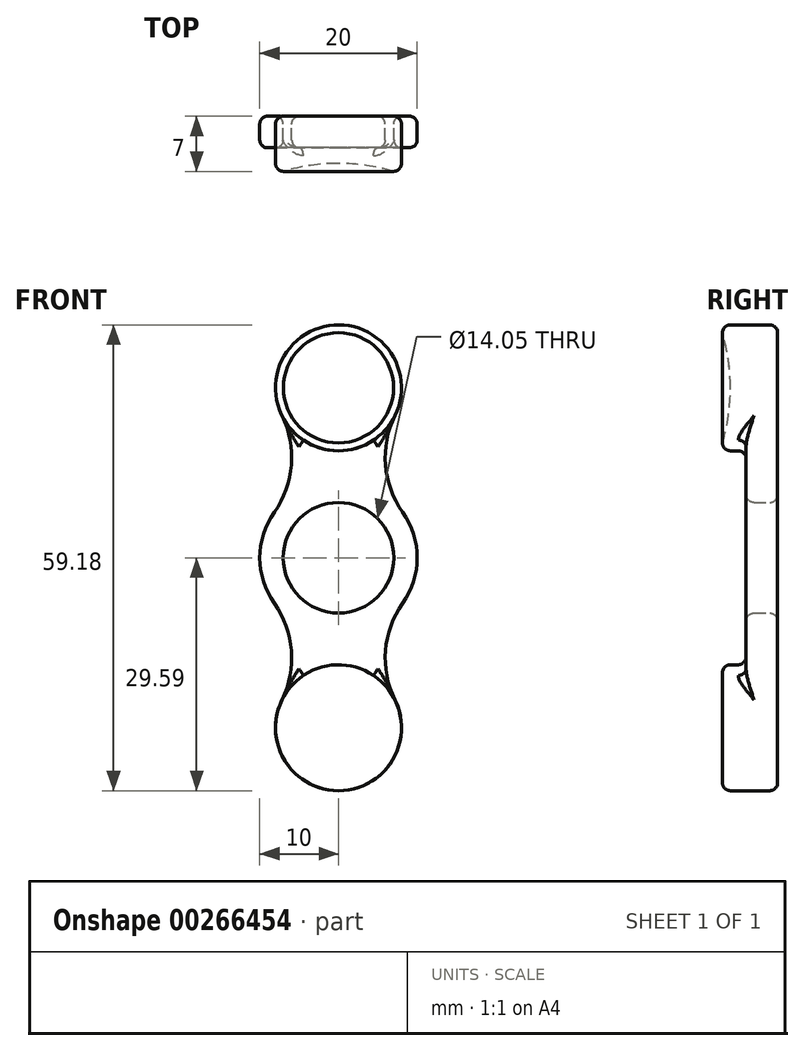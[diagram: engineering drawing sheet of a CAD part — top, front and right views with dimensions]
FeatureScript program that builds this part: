
annotation { "Feature Type Name" : "Feature", "Feature Type Description" : "" }
export const myFeature = defineFeature(function(context is Context, id is Id, definition is map)
    precondition{}
    {
        {
            var Q0;
            Q0=qCreatedBy(makeId("Front.planeOp"),FACE);
            var sketch = newSketch(context, id + "F7", { "sketchPlane" : qUnion([Q0])});
            skCircle(sketch, "E0", {"center": v(0, 0) * mm, "radius": 7.03 * mm});
            skArc(sketch, "E1", {"start": v(8.15, 5.8) * mm, "mid": v(10, 0) * mm, "end": v(8.15, -5.8) * mm});
            skLineSegment(sketch, "E2", {"start": v(0, 0) * mm, "end": v(0, 21.59) * mm, "construction": true});
            skArc(sketch, "E3", {"start": v(7.17, 18.05) * mm, "mid": v(0, 29.59) * mm, "end": v(-7.17, 18.05) * mm});
            skArc(sketch, "E4", {"start": v(-8.15, 5.8) * mm, "mid": v(-5.97, 11.79) * mm, "end": v(-7.17, 18.05) * mm});
            skArc(sketch, "E5.MirrorCS", {"start": v(8.15, 5.8) * mm, "mid": v(5.97, 11.79) * mm, "end": v(7.17, 18.05) * mm});
            skLineSegment(sketch, "E6", {"start": v(10, 0) * mm, "end": v(-10, 0) * mm, "construction": true});
            skArc(sketch, "E7.MirrorCS", {"start": v(7.17, -18.05) * mm, "mid": v(0, -29.59) * mm, "end": v(-7.17, -18.05) * mm});
            skArc(sketch, "E8.MirrorCS", {"start": v(-8.15, -5.8) * mm, "mid": v(-5.97, -11.79) * mm, "end": v(-7.17, -18.05) * mm});
            skArc(sketch, "E9.MirrorCS", {"start": v(8.15, -5.8) * mm, "mid": v(5.97, -11.79) * mm, "end": v(7.17, -18.05) * mm});
            skArc(sketch, "E10.trimOffspring", {"start": v(-8.15, -5.8) * mm, "mid": v(-10, 0) * mm, "end": v(-8.15, 5.8) * mm});
            skSolve(sketch);
        }
        {
            var Q0;
            Q0=makeQuery(id+"F7.imprint","IMPRINT",FACE,{"disambiguationData":[TD([[makeQuery(id+"F7.imprint","IMPRINT",EDGE,{"derivedFrom":sQuery(id+"F7.wireOp",EDGE,"E0")}),-1.0]])]});
            extrude(context, id + "F0", {"entities" : qUnion([Q0]), "depth" : 4 * mm});
        }
        {
            var Q0;
            Q0=makeQuery(id+"F0.opExtrude","CAP_FACE",FACE,{"disambiguationData":[OSD([sQuery(id+"F7.wireOp",EDGE,"E0"),sQuery(id+"F7.wireOp",EDGE,"E1"),sQuery(id+"F7.wireOp",EDGE,"E3"),sQuery(id+"F7.wireOp",EDGE,"E4"),sQuery(id+"F7.wireOp",EDGE,"E5.MirrorCS"),sQuery(id+"F7.wireOp",EDGE,"E7.MirrorCS"),sQuery(id+"F7.wireOp",EDGE,"E8.MirrorCS"),sQuery(id+"F7.wireOp",EDGE,"E9.MirrorCS"),sQuery(id+"F7.wireOp",EDGE,"E10.trimOffspring")])],"isStart":false});
            var sketch = newSketch(context, id + "F1", { "sketchPlane" : qUnion([Q0])});
            skCircle(sketch, "E11", {"center": v(0, -21.59) * mm, "radius": 8 * mm});
            skCircle(sketch, "E12", {"center": v(0, 21.59) * mm, "radius": 8 * mm});
            skSolve(sketch);
        }
        {
            var Q0;
            Q0 = qSketchRegion(id + "F1", true);
            extrude(context, id + "F2", {"entities" : qUnion([Q0]), "operationType" : NewBodyOperationType.ADD, "depth" : 3 * mm});
        }
        {
            var Q0;
            Q0=makeQuery(id+"F2.opExtrude","CAP_EDGE",EDGE,{"disambiguationData":[OSD([sQuery(id+"F1.wireOp",EDGE,"E12")])],"isStart":false});
            var Q1;
            Q1=makeQuery(id+"F2.opExtrude","CAP_EDGE",EDGE,{"disambiguationData":[OSD([sQuery(id+"F1.wireOp",EDGE,"E11")])],"isStart":false});
            fillet(context, id + "F3", {"entities" : qUnion([Q0, Q1]), "radius" : 1 * mm, "tangentPropagation" : true, "allowEdgeOverflow" : false});
        }
        {
            var Q0;
            Q0=makeQuery(id+"F0.opExtrude","CAP_FACE",FACE,{"disambiguationData":[OSD([sQuery(id+"F7.wireOp",EDGE,"E0"),sQuery(id+"F7.wireOp",EDGE,"E1"),sQuery(id+"F7.wireOp",EDGE,"E3"),sQuery(id+"F7.wireOp",EDGE,"E4"),sQuery(id+"F7.wireOp",EDGE,"E5.MirrorCS"),sQuery(id+"F7.wireOp",EDGE,"E7.MirrorCS"),sQuery(id+"F7.wireOp",EDGE,"E8.MirrorCS"),sQuery(id+"F7.wireOp",EDGE,"E9.MirrorCS"),sQuery(id+"F7.wireOp",EDGE,"E10.trimOffspring")])],"isStart":true});
            var Q1;
            Q1=makeQuery(id+"F0.opExtrude","CAP_FACE",FACE,{"disambiguationData":[OSD([sQuery(id+"F7.wireOp",EDGE,"E0"),sQuery(id+"F7.wireOp",EDGE,"E1"),sQuery(id+"F7.wireOp",EDGE,"E3"),sQuery(id+"F7.wireOp",EDGE,"E4"),sQuery(id+"F7.wireOp",EDGE,"E5.MirrorCS"),sQuery(id+"F7.wireOp",EDGE,"E7.MirrorCS"),sQuery(id+"F7.wireOp",EDGE,"E8.MirrorCS"),sQuery(id+"F7.wireOp",EDGE,"E9.MirrorCS"),sQuery(id+"F7.wireOp",EDGE,"E10.trimOffspring")])],"isStart":false});
            var Q2;
            Q2=makeQuery(id+"F0.opExtrude","CAP_EDGE",EDGE,{"disambiguationData":[OSD([sQuery(id+"F7.wireOp",EDGE,"E0")])],"isStart":false});
            var Q3;
            Q3=makeQuery(id+"F0.opExtrude","CAP_EDGE",EDGE,{"disambiguationData":[OSD([sQuery(id+"F7.wireOp",EDGE,"E0")])],"isStart":true});
            fillet(context, id + "F4", {"entities" : qUnion([Q0, Q1, Q2, Q3]), "radius" : 1 * mm, "tangentPropagation" : true, "allowEdgeOverflow" : false});
        }
        {
            var Q0;
            Q0=qCreatedBy(makeId("Right.planeOp"),FACE);
            var sketch = newSketch(context, id + "F5", { "sketchPlane" : qUnion([Q0])});
            skLineSegment(sketch, "E13.0", {"start": v(-7, 14.6) * mm, "end": v(-7, 28.59) * mm});
            skLineSegment(sketch, "E14", {"start": v(0, 0) * mm, "end": v(-21.03, 0) * mm, "construction": true});
            skLineSegment(sketch, "E15", {"start": v(-7, 21.59) * mm, "end": v(-6, 21.59) * mm});
            skPoint(sketch, "E15.endSnap0", {"position": v(-7, 21.59) * mm});
            skArc(sketch, "E16", {"start": v(-6, 21.59) * mm, "mid": v(-6.25, 25.13) * mm, "end": v(-7, 28.59) * mm});
            skLineSegment(sketch, "E17", {"start": v(-7, 21.59) * mm, "end": v(-31, 21.59) * mm, "construction": true});
            skSolve(sketch);
        }
        {
            var Q0;
            Q0 = qSketchRegion(id + "F5", true);
            var Q1;
            Q1=sQuery(id+"F5.wireOp",EDGE,"E17");
            revolve(context, id + "F6", {"operationType" : NewBodyOperationType.REMOVE, "entities" : qUnion([Q0]), "axis" : qUnion([Q1]), "revolveType" : RevolveType.FULL, "oppositeDirection" : true});
        }
    });
